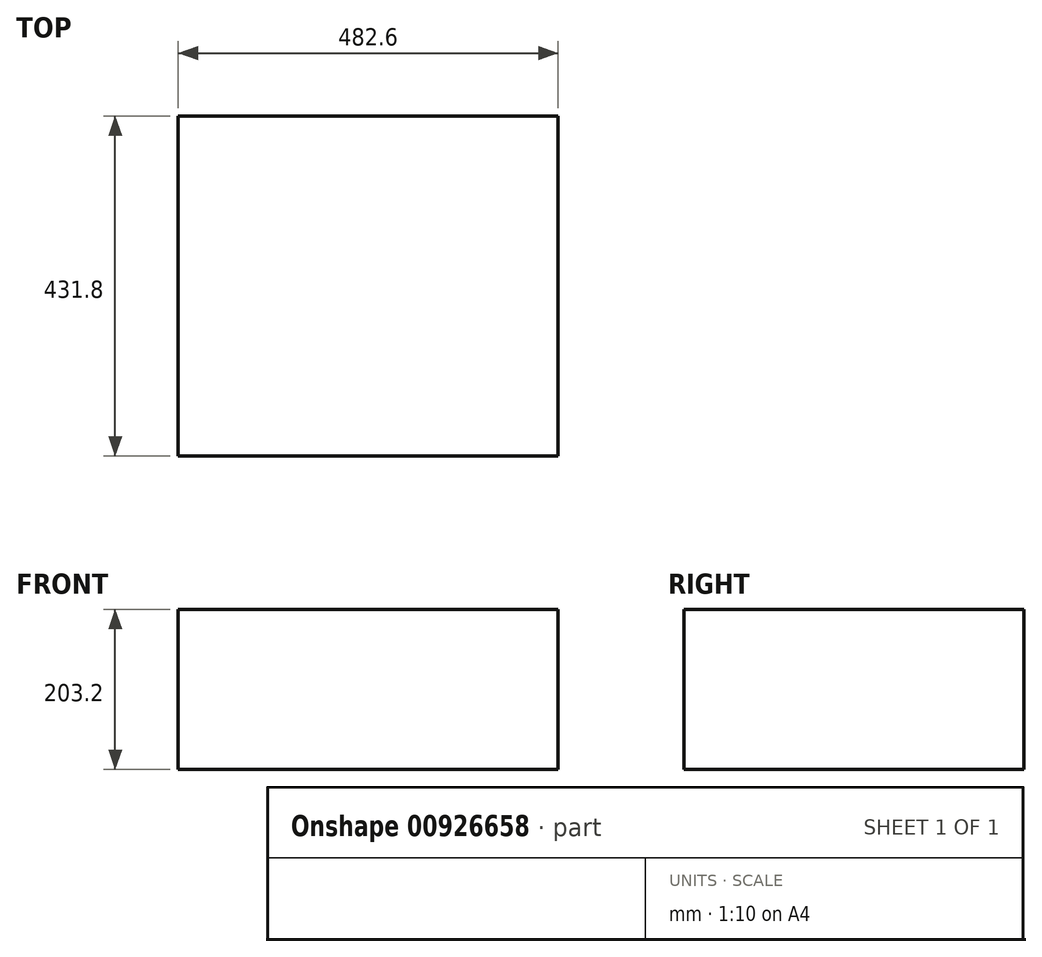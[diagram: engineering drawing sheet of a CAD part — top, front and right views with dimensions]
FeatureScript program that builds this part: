
annotation { "Feature Type Name" : "Feature", "Feature Type Description" : "" }
export const myFeature = defineFeature(function(context is Context, id is Id, definition is map)
    precondition{}
    {
        {
            var Q0;
            Q0=qCreatedBy(makeId("Top.planeOp"),FACE);
            var sketch = newSketch(context, id + "F0", { "sketchPlane" : qUnion([Q0])});
            skLineSegment(sketch, "E0.bottom", {"start": v(-238.17, 283.7) * mm, "end": v(244.43, 283.7) * mm});
            skLineSegment(sketch, "E0.top", {"start": v(-238.17, -148.1) * mm, "end": v(244.43, -148.1) * mm});
            skLineSegment(sketch, "E0.left", {"start": v(-238.17, 283.7) * mm, "end": v(-238.17, -148.1) * mm});
            skLineSegment(sketch, "E0.right", {"start": v(244.43, 283.7) * mm, "end": v(244.43, -148.1) * mm});
            skSolve(sketch);
        }
        {
            var Q0;
            Q0=makeQuery(id+"F0.imprint","IMPRINT",FACE,{"disambiguationData":[TD([[makeQuery(id+"F0.imprint","IMPRINT",EDGE,{"derivedFrom":sQuery(id+"F0.wireOp",EDGE,"E0.bottom")}),-1.0]])]});
            extrude(context, id + "F1", {"entities" : qUnion([Q0]), "depth" : 203.2 * mm, "offsetDistance" : 25.4 * mm});
        }
    });
